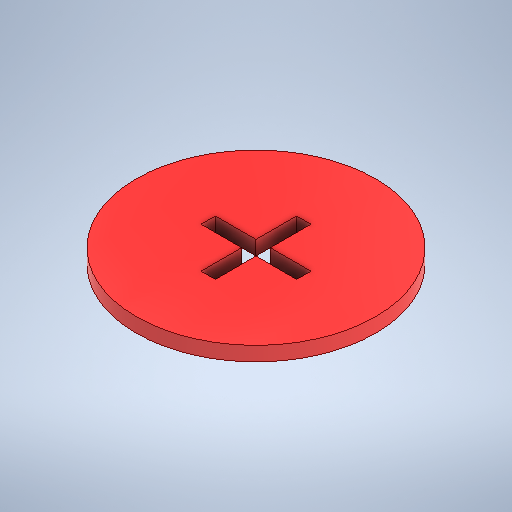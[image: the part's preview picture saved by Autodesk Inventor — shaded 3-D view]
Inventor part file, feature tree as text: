
AUTODESK INVENTOR PART (.ipt)
format: ipt  version: 2025 (Build 290162000, 162)  size: 248,832 bytes
history: native  units: mm
features: extrude x1, sketch x1
ambient origin geometry x8: Origin, YZ Plane, XZ Plane, XY Plane, X Axis, Y Axis, Z Axis, Center Point
bodies: Solid1 (feature_tree)
feature tree (2):
  extrude  "Extrusion1"  Depth=20.0mm
  sketch  "Sketch1"  dims[d0=50.0mm d1=20.0mm d2=3.0mm d3=1.5mm d4=10.0mm d5=3.0mm d6=20.0mm d7=10.0mm d8=1.5mm d9=3.0mm d10=0.0mm]
